# Revit family: BuroSeating_Buro Mentor Mesh
name_source: partatom
category: Furniture
units: mm (PartAtom-declared; Revit-internal decimal feet)

## family parameters
Always vertical = Yes
Cut with Voids When Loaded = No
OmniClass Number = 23.40.70.14.64.11
OmniClass Title = Office Furniture
Room Calculation Point = No
Shared = Yes
Work Plane-Based = No

## types (4) — shared parameters
ArmRestMaterial = BuroSeating_Plastic_Black
ArmRestSupportMaterial = BuroSeating_Aluminium_Black
Assembly Code = E2020
BackFrameMaterial = BuroSeating_Plastic_Black
BackPanelMaterial = BuroSeating_Fabric_Mesh_Black
BackRestMaterial = BuroSeating_Fabric_Mesh_Black
BackSupportMaterial = BuroSeating_Aluminium_Black
BaseMaterial = BuroSeating_Metal_Chrome_Semi-Polished
BottomLiftMaterial = BuroSeating_Plastic_Black
CastorMaterial = BuroSeating_Aluminium_Black
CastorWheelMaterial = BuroSeating_Aluminium_Black
FrameMaterial = BuroSeating_Aluminium_Black
HeadRestMaterial = BuroSeating_Fabric_Black
HeadRestSupportMaterial = BuroSeating_Plastic_Black
Manufacturer = Buro Seating
NominalDepth = 635 mm  [stored 2.08333 ft]
NominalHeight = 1210 mm
NominalSeatDepthRange = 430-480d
NominalSeatHeight = 475-595h
NominalWidth = 495 mm
ProductGroup = Mentor Mesh
ProductPageURL AU = https://buroseating.com
ProductPageURL NZ = https://buroseating.co.nz
ProductRange = Buro
SeatDepth = 455 mm
SeatLeverFrameMaterial = BuroSeating_Aluminium_Black
SeatLeverHandleMaterial = BuroSeating_Aluminium_Black
SeatMaterial = BuroSeating_Fabric_Mesh_Black
SeatSupportMaterial = BuroSeating_Aluminium_Black
SeatTiltMaterial = BuroSeating_Aluminium_Black
SeatWidth = 520 mm
TopLiftMaterial = BuroSeating_Metal_Chrome_Semi-Polished
Type Comments = Seat Height 475-595mm High
URL = https://buroseating.co.nz
URL AU = https://buroseating.com
WarrantyDescription = Full 5 year guarantee (excluding upholstery)
zero-valued in all types: Default Elevation

## per-type parameters (varying)
| type | Description | Model | SeatArms | SeatHeadRest |
| Buro Mentor Mesh 132A-M3 | Buro Mentor Mesh | Buro Mentor Mesh 132A-M3 | No | No |
| Buro Mentor Mesh 132A-M3 with Arms | Buro Mentor Mesh with Arms | 159-M3 | Yes | No |
| Buro Mentor Mesh 132A-M3 with Headrest | Buro Mentor Mesh with Head Rest | 159-M3 | No | Yes |
| Buro Mentor Mesh 132A-M3 with Arms and Headrest | Buro Mentor Mesh with Arms and Headrest | 159-M3 | Yes | Yes |

note: [stored X ft] marks values corroborated as IEEE doubles in the binary element streams (Revit-internal decimal feet)

## geometry (parser evidence)
native form markers: Sweep x6
no freeform markers — native parametric forms only
